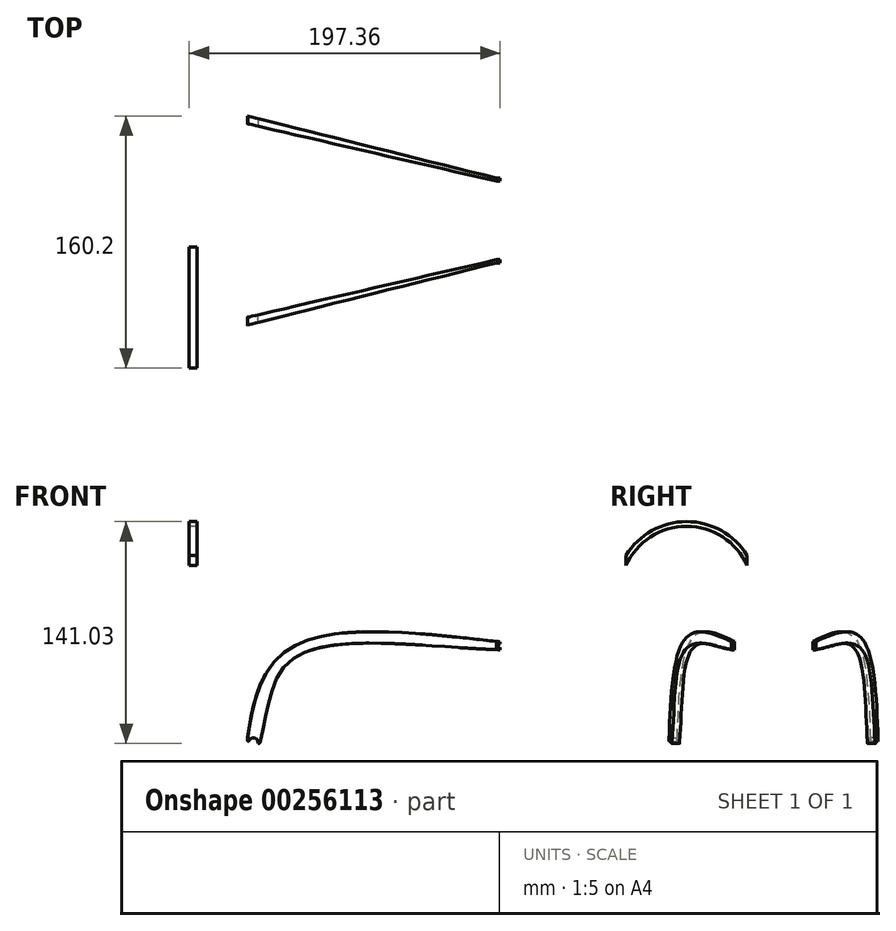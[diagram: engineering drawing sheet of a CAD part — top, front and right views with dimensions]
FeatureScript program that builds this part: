
annotation { "Feature Type Name" : "Feature", "Feature Type Description" : "" }
export const myFeature = defineFeature(function(context is Context, id is Id, definition is map)
    precondition{}
    {
        {
            var Q0;
            Q0=qCreatedBy(makeId("Front.planeOp"),FACE);
            var sketch = newSketch(context, id + "F0", { "sketchPlane" : qUnion([Q0])});
            skLineSegment(sketch, "E0", {"start": v(-44.38, -66.5) * mm, "end": v(-44.38, -56.5) * mm});
            skLineSegment(sketch, "E1", {"start": v(-44.38, -66.5) * mm, "end": v(-19.38, -66.5) * mm});
            skLineSegment(sketch, "E2", {"start": v(-19.38, -66.5) * mm, "end": v(-19.38, -49.72) * mm});
            skLineSegment(sketch, "E3", {"start": v(-19.38, -66.5) * mm, "end": v(-19.38, 58.5) * mm});
            skFitSpline(sketch, "E4", {"points": [v(-44.38, -56.5) * mm, v(-57.22, -43.17) * mm, v(-68.05, -20.03) * mm, v(-74.38, 11.73) * mm, v(-67.31, 46.93) * mm, v(-49.84, 57.51) * mm, v(-19.38, 58.5) * mm], "startDerivative": vector(-110.67, 66.78) * mm, "endDerivative": vector(182, -6.38) * mm});
            skLineSegment(sketch, "E5.0", {"start": v(-46.38, -66.5) * mm, "end": v(-46.38, -59.39) * mm});
            skFitSpline(sketch, "E6.0", {"points": [v(-46.19, -59.5) * mm, v(-48.77, -57.94) * mm, v(-52.27, -55.1) * mm, v(-56.3, -50.55) * mm, v(-59.07, -46.8) * mm, v(-61.63, -42.78) * mm, v(-64.02, -38.5) * mm, v(-66.25, -33.97) * mm, v(-68.32, -29.25) * mm, v(-69.92, -25.18) * mm, v(-71.12, -21.86) * mm, v(-72.28, -18.5) * mm, v(-73.65, -14.21) * mm, v(-75.09, -8.88) * mm, v(-76.29, -3.33) * mm, v(-77.2, 2.45) * mm, v(-77.7, 7.48) * mm, v(-77.9, 11.64) * mm, v(-77.97, 15.9) * mm, v(-77.8, 21.34) * mm, v(-77.15, 27.87) * mm, v(-76.04, 34.23) * mm, v(-74.68, 39.23) * mm, v(-73.3, 42.97) * mm, v(-72.12, 45.63) * mm, v(-70.98, 47.7) * mm, v(-69.98, 49.26) * mm, v(-68.92, 50.73) * mm, v(-67.49, 52.43) * mm, v(-65, 54.83) * mm, v(-61.53, 57.24) * mm, v(-56.97, 59.3) * mm, v(-52.94, 60.46) * mm, v(-49.6, 61.14) * mm, v(-46.16, 61.67) * mm, v(-41.74, 62.1) * mm, v(-36.26, 62.32) * mm, v(-28.77, 62.33) * mm, v(-23.05, 62.13) * mm, v(-19.26, 62) * mm]});
            skLineSegment(sketch, "E7", {"start": v(-44.38, -66.5) * mm, "end": v(-46.38, -66.5) * mm});
            skLineSegment(sketch, "E8", {"start": v(-19.38, 58.5) * mm, "end": v(-19.26, 62) * mm});
            skFitSpline(sketch, "E9.MirrorCS", {"points": [v(5.62, -56.5) * mm, v(18.46, -43.17) * mm, v(29.3, -20.03) * mm, v(35.62, 11.73) * mm, v(28.55, 46.93) * mm, v(11.07, 57.51) * mm, v(-19.38, 58.5) * mm], "startDerivative": vector(110.67, 66.78) * mm, "endDerivative": vector(-182, -6.38) * mm});
            skLineSegment(sketch, "E10.MirrorCS", {"start": v(7.62, -66.5) * mm, "end": v(7.62, -59.39) * mm});
            skLineSegment(sketch, "E11.MirrorCS", {"start": v(5.62, -66.5) * mm, "end": v(7.62, -66.5) * mm});
            skLineSegment(sketch, "E12.MirrorCS", {"start": v(5.62, -66.5) * mm, "end": v(5.62, -56.5) * mm});
            skLineSegment(sketch, "E13.MirrorCS", {"start": v(-19.38, 58.5) * mm, "end": v(-19.5, 62) * mm});
            skFitSpline(sketch, "E14.0", {"points": [v(7.43, -59.5) * mm, v(10.01, -57.94) * mm, v(13.5, -55.1) * mm, v(17.54, -50.55) * mm, v(20.31, -46.8) * mm, v(22.87, -42.78) * mm, v(25.26, -38.5) * mm, v(27.49, -33.97) * mm, v(29.56, -29.25) * mm, v(31.16, -25.18) * mm, v(32.36, -21.86) * mm, v(33.52, -18.5) * mm, v(34.88, -14.21) * mm, v(36.33, -8.88) * mm, v(37.53, -3.33) * mm, v(38.45, 2.45) * mm, v(38.93, 7.48) * mm, v(39.14, 11.64) * mm, v(39.2, 15.9) * mm, v(39.04, 21.34) * mm, v(38.4, 27.87) * mm, v(37.28, 34.23) * mm, v(35.92, 39.23) * mm, v(34.54, 42.97) * mm, v(33.36, 45.63) * mm, v(32.22, 47.7) * mm, v(31.22, 49.26) * mm, v(30.16, 50.73) * mm, v(28.73, 52.43) * mm, v(26.23, 54.83) * mm, v(22.77, 57.24) * mm, v(18.21, 59.3) * mm, v(14.18, 60.46) * mm, v(10.83, 61.14) * mm, v(7.4, 61.67) * mm, v(2.98, 62.1) * mm, v(-2.5, 62.32) * mm, v(-9.99, 62.33) * mm, v(-15.71, 62.13) * mm, v(-19.5, 62) * mm]});
            skSolve(sketch);
        }
        {
            var Q0;
            Q0=makeQuery(id+"F0.imprint","IMPRINT",FACE,{"disambiguationData":[TD([[makeQuery(id+"F0.imprint","IMPRINT",EDGE,{"derivedFrom":sQuery(id+"F0.wireOp",EDGE,"E0")}),1.0]])]});
            var Q1;
            {var subQ1=sQuery(id+"F0.wireOp",EDGE,"E8");Q1=makeQuery(id+"F0.imprint","IMPRINT",FACE,{"disambiguationData":[TD([[makeQuery(id+"F0.imprint","IMPRINT",EDGE,{"derivedFrom":subQ1}),-1.0]])]});}
            var Q2;
            {var subQ0=sQuery(id+"F0.wireOp",EDGE,"E8");Q2=makeQuery(id+"F0.imprint","IMPRINT",FACE,{"disambiguationData":[TD([[makeQuery(id+"F0.imprint","IMPRINT",EDGE,{"derivedFrom":subQ0}),1.0]])]});}
            extrude(context, id + "F1", {"entities" : qUnion([Q0, Q1, Q2]), "depth" : 5 * mm});
        }
        {
            var Q0;
            Q0=makeQuery(id+"F1.opExtrude","SWEPT_FACE",FACE,{"disambiguationData":[OSD([sQuery(id+"F0.wireOp",EDGE,"E5.0")])]});
            var sketch = newSketch(context, id + "F2", { "sketchPlane" : qUnion([Q0])});
            skCircle(sketch, "E15", {"center": v(2.5, -63.7) * mm, "radius": 1.15 * mm});
            skPoint(sketch, "E15.centerSnap0", {"position": v(2.5, -66.5) * mm});
            skSolve(sketch);
        }
        {
            var Q0;
            Q0=makeQuery(id+"F2.imprint","IMPRINT",FACE,{"disambiguationData":[TD([[makeQuery(id+"F2.imprint","IMPRINT",EDGE,{"derivedFrom":sQuery(id+"F2.wireOp",EDGE,"E15")}),1.0]])]});
            extrude(context, id + "F3", {"entities" : qUnion([Q0]), "operationType" : NewBodyOperationType.REMOVE, "endBound" : BoundingType.THROUGH_ALL, "oppositeDirection" : true, "depth" : 25 * mm});
        }
        {
            var Q0;
            Q0=makeQuery(id+"F1.opExtrude","CAP_EDGE",EDGE,{"disambiguationData":[OSD([sQuery(id+"F0.wireOp",EDGE,"E7")])],"isStart":true});
            var Q1;
            Q1=makeQuery(id+"F1.opExtrude","CAP_EDGE",EDGE,{"disambiguationData":[OSD([sQuery(id+"F0.wireOp",EDGE,"E7")])],"isStart":false});
            var Q2;
            Q2=makeQuery(id+"F1.opExtrude","CAP_EDGE",EDGE,{"disambiguationData":[OSD([sQuery(id+"F0.wireOp",EDGE,"E11.MirrorCS")])],"isStart":true});
            var Q3;
            Q3=makeQuery(id+"F1.opExtrude","CAP_EDGE",EDGE,{"disambiguationData":[OSD([sQuery(id+"F0.wireOp",EDGE,"E11.MirrorCS")])],"isStart":false});
            fillet(context, id + "F4", {"entities" : qUnion([Q0, Q1, Q2, Q3]), "radius" : 2.5 * mm, "tangentPropagation" : true, "allowEdgeOverflow" : false});
        }
        {
            var Q0;
            Q0=qCreatedBy(makeId("Front.planeOp"),FACE);
            var sketch = newSketch(context, id + "F5", { "sketchPlane" : qUnion([Q0])});
            skCircle(sketch, "E16", {"center": v(94.28, 11.46) * mm, "radius": 5.15 * mm});
            skSolve(sketch);
        }
        {
            var Q0;
            Q0=makeQuery(id+"F5.imprint","IMPRINT",FACE,{"disambiguationData":[TD([[makeQuery(id+"F5.imprint","IMPRINT",EDGE,{"derivedFrom":sQuery(id+"F5.wireOp",EDGE,"E16")}),1.0]])]});
            extrude(context, id + "F6", {"entities" : qUnion([Q0]), "depth" : 4.5 * mm});
        }
        {
            var Q0;
            Q0=makeQuery(id+"F6.opExtrude","CAP_FACE",FACE,{"disambiguationData":[OSD([sQuery(id+"F5.wireOp",EDGE,"E16")])],"isStart":false});
            shell(context, id + "F7", {"entities" : qUnion([Q0]), "thickness" : 1 * mm, "oppositeDirection" : true});
        }
        {
            var Q0;
            Q0=qCreatedBy(makeId("Front.planeOp"),FACE);
            var sketch = newSketch(context, id + "F8", { "sketchPlane" : qUnion([Q0])});
            skCircle(sketch, "E17", {"center": v(267.16, -183) * mm, "radius": 1.15 * mm});
            skLineSegment(sketch, "E18", {"start": v(267.16, -183) * mm, "end": v(267.16, -180.5) * mm});
            skLineSegment(sketch, "E19", {"start": v(267.16, -180.5) * mm, "end": v(267.16, -185.5) * mm});
            skLineSegment(sketch, "E20", {"start": v(113.46, -245.1) * mm, "end": v(113.4, -245.1) * mm});
            skFitSpline(sketch, "E21", {"points": [v(267.16, -185.5) * mm, v(134.84, -191.88) * mm, v(114.38, -245.32) * mm], "startDerivative": vector(-251.28, 8.33) * mm, "endDerivative": vector(-40.13, -135.71) * mm});
            skFitSpline(sketch, "E22", {"points": [v(267.16, -180.5) * mm, v(132.38, -185.5) * mm, v(106.58, -243.54) * mm], "startDerivative": vector(-282.9, 31.95) * mm, "endDerivative": vector(-21.7, -168.96) * mm});
            skArc(sketch, "E23", {"start": v(113.4, -245.1) * mm, "mid": v(111.14, -241.5) * mm, "end": v(107.55, -243.76) * mm});
            skLineSegment(sketch, "E24.0", {"start": v(269.66, -183) * mm, "end": v(269.66, -183) * mm});
            skLineSegment(sketch, "E25", {"start": v(267.16, -180.5) * mm, "end": v(267.16, -180.5) * mm});
            skLineSegment(sketch, "E26", {"start": v(267.16, -185.5) * mm, "end": v(267.16, -185.5) * mm});
            skPoint(sketch, "E27.visualSharp", {"position": v(269.66, -180.5) * mm});
            skArc(sketch, "E27.filletArc", {"start": v(269.66, -183) * mm, "mid": v(268.95, -181.26) * mm, "end": v(267.24, -180.5) * mm});
            skPoint(sketch, "E28.visualSharp", {"position": v(269.66, -185.5) * mm});
            skArc(sketch, "E28.filletArc", {"start": v(267.16, -185.5) * mm, "mid": v(268.92, -184.76) * mm, "end": v(269.66, -183) * mm});
            skArc(sketch, "E29.filletArc", {"start": v(267.04, -180.48) * mm, "mid": v(267.14, -180.5) * mm, "end": v(267.24, -180.5) * mm});
            skArc(sketch, "E30.filletArc", {"start": v(106.7, -242.64) * mm, "mid": v(106.87, -243.34) * mm, "end": v(107.46, -243.74) * mm});
            skArc(sketch, "E31.filletArc", {"start": v(113.46, -245.1) * mm, "mid": v(114.2, -245) * mm, "end": v(114.64, -244.4) * mm});
            skLineSegment(sketch, "E32.trimOffspring", {"start": v(107.55, -243.76) * mm, "end": v(107.46, -243.74) * mm});
            skSolve(sketch);
        }
        {
            var Q0;
            Q0=qCreatedBy(makeId("Top.planeOp"),FACE);
            var sketch = newSketch(context, id + "F9", { "sketchPlane" : qUnion([Q0])});
            skLineSegment(sketch, "E33", {"start": v(278.28, -4.67) * mm, "end": v(264.78, -4.67) * mm});
            skLineSegment(sketch, "E34", {"start": v(264.78, -4.67) * mm, "end": v(104.78, -41.67) * mm});
            skLineSegment(sketch, "E35", {"start": v(264.78, -4.67) * mm, "end": v(104.78, -4.67) * mm});
            skLineSegment(sketch, "E36", {"start": v(104.78, -4.67) * mm, "end": v(104.78, -41.67) * mm});
            skLineSegment(sketch, "E37", {"start": v(104.78, -41.67) * mm, "end": v(104.78, -46.67) * mm});
            skLineSegment(sketch, "E38", {"start": v(104.78, -46.67) * mm, "end": v(264.78, -6.67) * mm});
            skLineSegment(sketch, "E39", {"start": v(264.78, -6.67) * mm, "end": v(278.28, -6.67) * mm});
            skLineSegment(sketch, "E40", {"start": v(278.28, -6.67) * mm, "end": v(278.28, -4.67) * mm});
            skSolve(sketch);
        }
        {
            var Q0;
            Q0=makeQuery(id+"F9.imprint","IMPRINT",FACE,{"disambiguationData":[TD([[makeQuery(id+"F9.imprint","IMPRINT",EDGE,{"derivedFrom":sQuery(id+"F9.wireOp",EDGE,"E33")}),1.0]])]});
            extrude(context, id + "F10", {"entities" : qUnion([Q0]), "oppositeDirection" : true, "depth" : 330 * mm});
        }
        {
            var Q0;
            Q0=makeQuery(id+"F8.imprint","IMPRINT",FACE,{"disambiguationData":[TD([[makeQuery(id+"F8.imprint","IMPRINT",EDGE,{"derivedFrom":sQuery(id+"F8.wireOp",EDGE,"E20")}),-1.0]])]});
            extrude(context, id + "F11", {"entities" : qUnion([Q0]), "operationType" : NewBodyOperationType.INTERSECT, "depth" : 102.6 * mm});
        }
        {
            var Q0;
            Q0=makeQuery(id+"F10.opExtrude","SWEPT_BODY",BODY,{"disambiguationData":[OSD([sQuery(id+"F9.wireOp",EDGE,"E33"),sQuery(id+"F9.wireOp",EDGE,"E34"),sQuery(id+"F9.wireOp",EDGE,"E37"),sQuery(id+"F9.wireOp",EDGE,"E38"),sQuery(id+"F9.wireOp",EDGE,"E39"),sQuery(id+"F9.wireOp",EDGE,"E40")])]});
            transform(context, id + "F12", {"entities" : qUnion([Q0]), "transformType" : TransformType.TRANSLATION_3D, "dx" : -69.8 * mm, "dy" : -27.2 * mm, "dz" : 146 * mm, "makeCopy" : false});
        }
        {
            var Q0;
            Q0=makeQuery(id+"F10.opExtrude","SWEPT_BODY",BODY,{"disambiguationData":[OSD([sQuery(id+"F9.wireOp",EDGE,"E33"),sQuery(id+"F9.wireOp",EDGE,"E34"),sQuery(id+"F9.wireOp",EDGE,"E37"),sQuery(id+"F9.wireOp",EDGE,"E38"),sQuery(id+"F9.wireOp",EDGE,"E39"),sQuery(id+"F9.wireOp",EDGE,"E40")])]});
            var Q1;
            Q1=qCreatedBy(makeId("Front.planeOp"),FACE);
            mirror(context, id + "F13", {"entities" : qUnion([Q0]), "mirrorPlane" : qUnion([Q1])});
        }
        {
            var Q0;
            Q0=makeQuery(id+"F13.opPattern","COPY",BODY,{"derivedFrom":makeQuery(id+"F10.opExtrude","SWEPT_BODY",BODY,{"disambiguationData":[OSD([sQuery(id+"F9.wireOp",EDGE,"E33"),sQuery(id+"F9.wireOp",EDGE,"E34"),sQuery(id+"F9.wireOp",EDGE,"E37"),sQuery(id+"F9.wireOp",EDGE,"E38"),sQuery(id+"F9.wireOp",EDGE,"E39"),sQuery(id+"F9.wireOp",EDGE,"E40")])]}),"instanceName":"1"});
            transform(context, id + "F14", {"entities" : qUnion([Q0]), "transformType" : TransformType.TRANSLATION_3D, "dx" : 0 * mm, "dy" : -13.9 * mm, "dz" : 0 * mm, "makeCopy" : false});
        }
        {
            var Q0;
            Q0=qCreatedBy(makeId("Right.planeOp"),FACE);
            var sketch = newSketch(context, id + "F15", { "sketchPlane" : qUnion([Q0])});
            skLineSegment(sketch, "E41", {"start": v(-23.71, 13.9) * mm, "end": v(-100.71, 13.9) * mm});
            skArc(sketch, "E42", {"start": v(-23.71, 13.9) * mm, "mid": v(-62.21, 38.9) * mm, "end": v(-100.71, 13.9) * mm});
            skLineSegment(sketch, "E43", {"start": v(-100.71, 13.9) * mm, "end": v(-100.71, 20.33) * mm});
            skLineSegment(sketch, "E44", {"start": v(-23.71, 13.9) * mm, "end": v(-23.71, 20.33) * mm});
            skArc(sketch, "E45.0", {"start": v(-23.71, 20.33) * mm, "mid": v(-62.21, 41.9) * mm, "end": v(-100.71, 20.33) * mm});
            skSolve(sketch);
        }
        {
            var Q0;
            Q0=makeQuery(id+"F15.imprint","IMPRINT",FACE,{"disambiguationData":[TD([[makeQuery(id+"F15.imprint","IMPRINT",EDGE,{"derivedFrom":sQuery(id+"F15.wireOp",EDGE,"E42")}),-1.0]])]});
            extrude(context, id + "F16", {"entities" : qUnion([Q0]), "depth" : 5 * mm});
        }
    });
